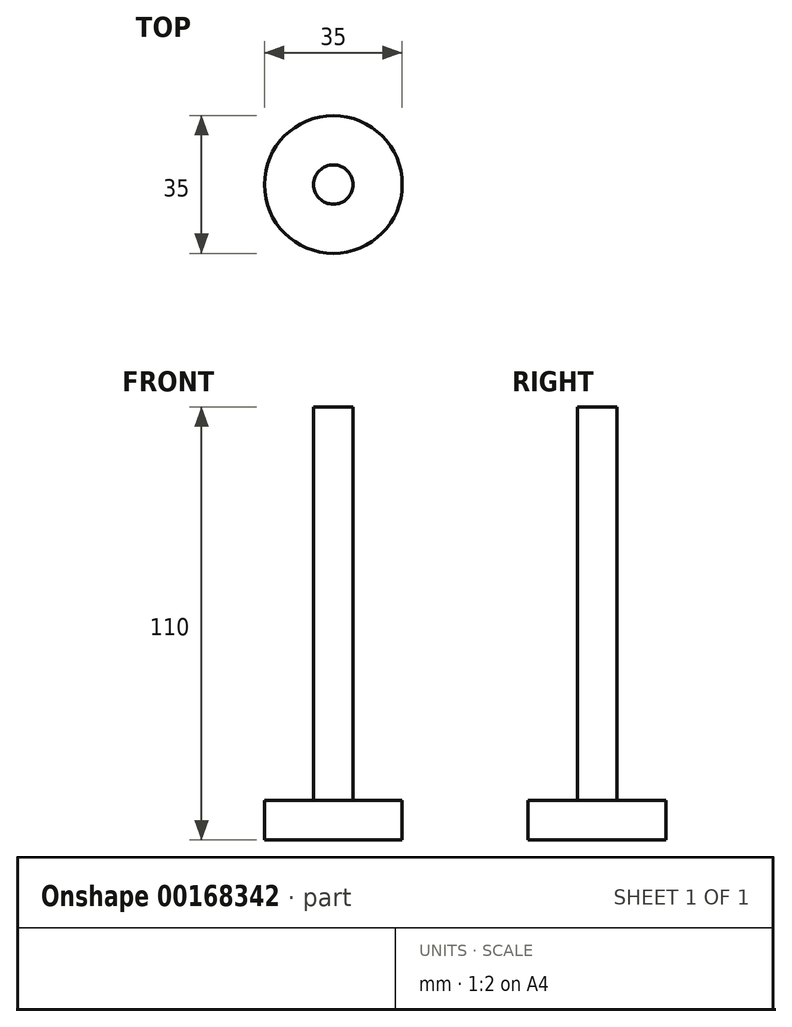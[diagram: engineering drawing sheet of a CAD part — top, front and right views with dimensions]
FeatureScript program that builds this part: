
annotation { "Feature Type Name" : "Feature", "Feature Type Description" : "" }
export const myFeature = defineFeature(function(context is Context, id is Id, definition is map)
    precondition{}
    {
        {
            var Q0;
            Q0=qCreatedBy(makeId("Top.planeOp"),FACE);
            var sketch = newSketch(context, id + "F0", { "sketchPlane" : qUnion([Q0])});
            skCircle(sketch, "E0", {"center": v(0, 0) * mm, "radius": 17.5 * mm});
            skSolve(sketch);
        }
        {
            var Q0;
            Q0=makeQuery(id+"F0.imprint","IMPRINT",FACE,{"disambiguationData":[TD([[makeQuery(id+"F0.imprint","IMPRINT",EDGE,{"derivedFrom":sQuery(id+"F0.wireOp",EDGE,"E0")}),1.0]])]});
            extrude(context, id + "F1", {"entities" : qUnion([Q0]), "oppositeDirection" : true, "depth" : 10 * mm});
        }
        {
            var Q0;
            Q0=makeQuery(id+"F1.opExtrude","CAP_FACE",FACE,{"disambiguationData":[OSD([sQuery(id+"F0.wireOp",EDGE,"E0")])],"isStart":true});
            var sketch = newSketch(context, id + "F2", { "sketchPlane" : qUnion([Q0])});
            skCircle(sketch, "E1", {"center": v(0, 0) * mm, "radius": 5 * mm});
            skSolve(sketch);
        }
        {
            var Q0;
            Q0=makeQuery(id+"F2.imprint","IMPRINT",FACE,{"disambiguationData":[TD([[makeQuery(id+"F2.imprint","IMPRINT",EDGE,{"derivedFrom":sQuery(id+"F2.wireOp",EDGE,"E1")}),1.0]])]});
            extrude(context, id + "F3", {"entities" : qUnion([Q0]), "operationType" : NewBodyOperationType.ADD, "depth" : 100 * mm});
        }
    });
